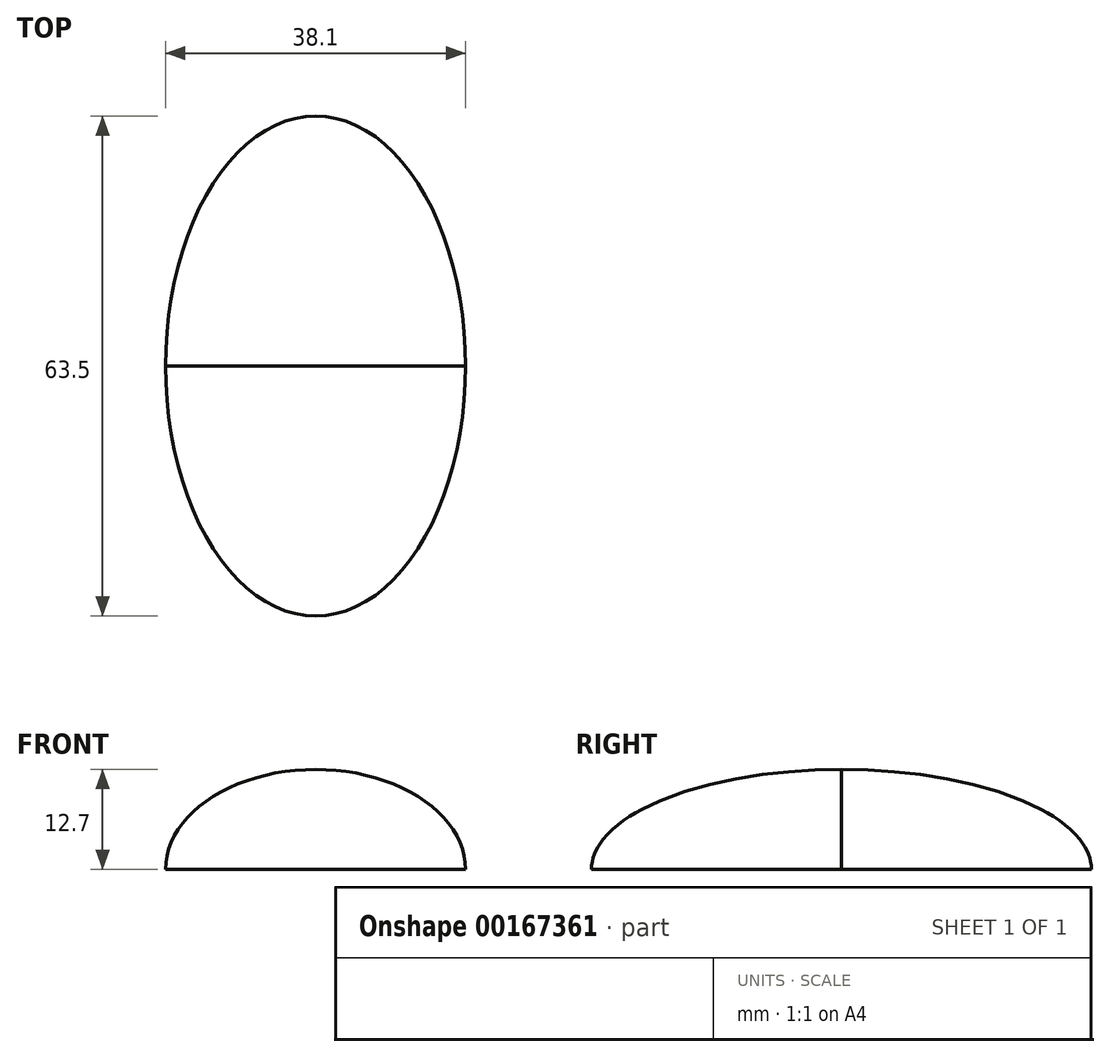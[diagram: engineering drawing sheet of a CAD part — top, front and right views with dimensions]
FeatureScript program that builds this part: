
annotation { "Feature Type Name" : "Feature", "Feature Type Description" : "" }
export const myFeature = defineFeature(function(context is Context, id is Id, definition is map)
    precondition{}
    {
        {
            var Q0;
            Q0=qCreatedBy(makeId("Top.planeOp"),FACE);
            var sketch = newSketch(context, id + "F0", { "sketchPlane" : qUnion([Q0])});
            skEllipse(sketch, "E0", {"center": v(0, 0) * mm, "majorRadius": 31.75 * mm, "minorRadius": 19.05 * mm, "majorAxis": v(0, 1)});
            skLineSegment(sketch, "E1", {"start": v(19.05, 0) * mm, "end": v(-19.05, 0) * mm});
            skSolve(sketch);
        }
        {
            var Q0;
            Q0=qCreatedBy(makeId("Right.planeOp"),FACE);
            var sketch = newSketch(context, id + "F1", { "sketchPlane" : qUnion([Q0])});
            skEllipticalArc(sketch, "E2", {});
            skLineSegment(sketch, "E3", {"start": v(-31.75, 0) * mm, "end": v(31.75, 0) * mm});
            skLineSegment(sketch, "E4", {"start": v(0, 0) * mm, "end": v(0, 12.7) * mm});
            skEllipticalArc(sketch, "E5.MirrorCS", {});
            const initialGuessF1  = {"E2": [0, 0, -1, 0, 0.03175, 0.0127, 3.141592653589793, 4.71238898038469], "E5.MirrorCS": [0, 0, 1, 0, 0.03175, 0.0127, 1.5707963267948966, 3.141592653589793]};
            skSetInitialGuess(sketch, initialGuessF1);
            skSolve(sketch);
        }
        {
            var Q0;
            Q0=qCreatedBy(makeId("Front.planeOp"),FACE);
            var sketch = newSketch(context, id + "F2", { "sketchPlane" : qUnion([Q0])});
            skEllipticalArc(sketch, "E6", {});
            skLineSegment(sketch, "E7", {"start": v(-19.05, 0) * mm, "end": v(19.05, 0) * mm});
            const initialGuessF2  = {"E6": [0, 0, 1, 0, 0.01905, 0.0127, 0, 3.141592653589793]};
            skSetInitialGuess(sketch, initialGuessF2);
            skSolve(sketch);
        }
        {
            var Q0;
            Q0=makeQuery(id+"F2.imprint","IMPRINT",FACE,{"disambiguationData":[TD([[makeQuery(id+"F2.imprint","IMPRINT",EDGE,{"derivedFrom":sQuery(id+"F2.wireOp",EDGE,"E6")}),1.0]])]});
            var Q1;
            {var subQ0=sQuery(id+"F0.wireOp",EDGE,"E1");Q1=makeQuery(id+"F0.imprint","IMPRINT",FACE,{"disambiguationData":[TD([[makeQuery(id+"F0.imprint","IMPRINT",EDGE,{"derivedFrom":subQ0}),-1.0]])]});}
            var Q2;
            Q2=sQuery(id+"F1.wireOp",EDGE,"E2");
            loft(context, id + "F3", {"addGuides" : true, "sheetProfilesArray" : [{ "sheetProfileEntities" : qUnion([Q0]) }, { "sheetProfileEntities" : qUnion([Q1]) }], "guidesArray" : [{ "guideEntities" : qUnion([Q2]), "guideDerivativeType" : LoftGuideDerivativeType.DEFAULT, "guideDerivativeMagnitude" : 1 }]});
        }
        {
            var Q1;
            Q1=makeQuery(id+"F2.imprint","IMPRINT",FACE,{"disambiguationData":[TD([[makeQuery(id+"F2.imprint","IMPRINT",EDGE,{"derivedFrom":sQuery(id+"F2.wireOp",EDGE,"E6")}),1.0]])]});
            var Q2;
            {var subQ0=sQuery(id+"F0.wireOp",EDGE,"E1");Q2=makeQuery(id+"F0.imprint","IMPRINT",FACE,{"disambiguationData":[TD([[makeQuery(id+"F0.imprint","IMPRINT",EDGE,{"derivedFrom":subQ0}),1.0]])]});}
            var Q3;
            Q3=sQuery(id+"F1.wireOp",EDGE,"E5.MirrorCS");
            loft(context, id + "F4", {"operationType" : NewBodyOperationType.ADD, "addGuides" : true, "sheetProfilesArray" : [{ "sheetProfileEntities" : qUnion([Q1]) }, { "sheetProfileEntities" : qUnion([Q2]) }], "guidesArray" : [{ "guideEntities" : qUnion([Q3]), "guideDerivativeType" : LoftGuideDerivativeType.DEFAULT, "guideDerivativeMagnitude" : 1 }]});
        }
    });
